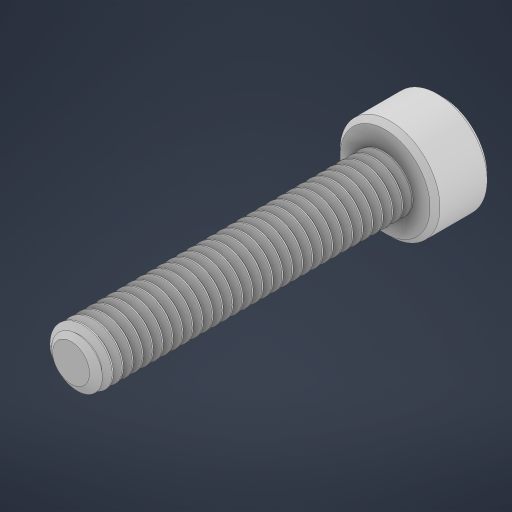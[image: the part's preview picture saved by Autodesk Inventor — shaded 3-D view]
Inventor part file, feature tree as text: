
AUTODESK INVENTOR PART (.ipt)
format: ipt  version: 2023 (Build 270158000, 158)  size: 1,118,208 bytes
history: native  units: in
note: dims shown in document units (in); Inventor stores cm internally (conversion verified against a paired STEP export)
features: chamfer x1
ambient origin geometry x8: Origin, YZ Plane, XZ Plane, XY Plane, X Axis, Y Axis, Z Axis, Center Point
bodies: Solid1 (feature_tree)
feature tree (1):
  chamfer  "Chamfer1"  [1 undecoded]
note: 1 required parameter value undecoded (feature->parameter linkage not recoverable at this tier; creation-order binding heuristic only, values carry confidence <= 0.55)
